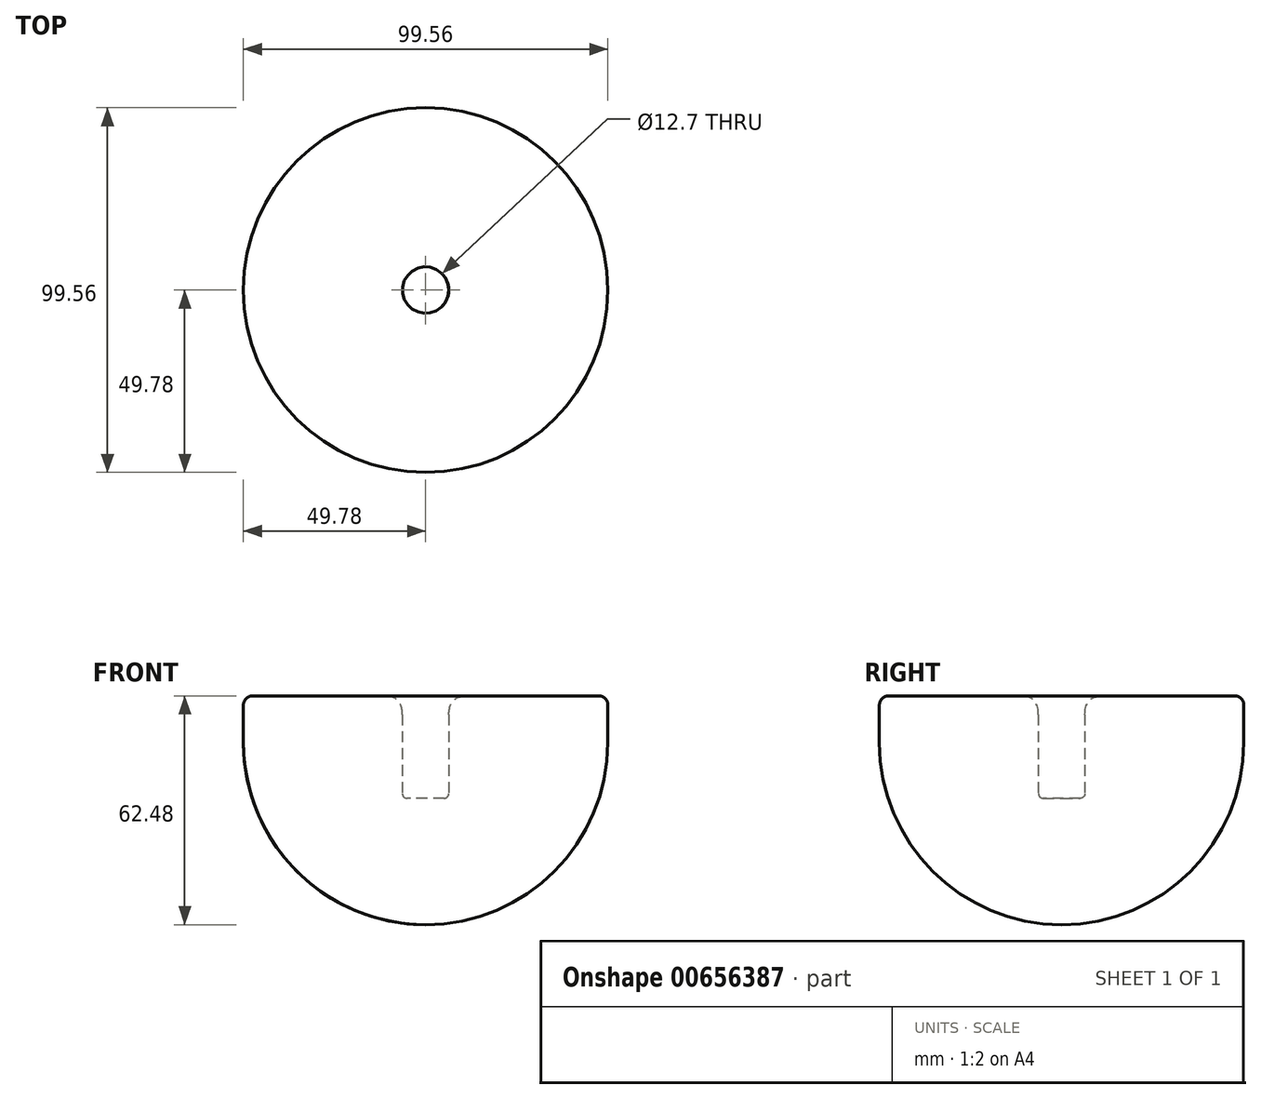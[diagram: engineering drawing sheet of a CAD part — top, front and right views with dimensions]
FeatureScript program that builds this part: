
annotation { "Feature Type Name" : "Feature", "Feature Type Description" : "" }
export const myFeature = defineFeature(function(context is Context, id is Id, definition is map)
    precondition{}
    {
        {
            var Q0;
            Q0=qCreatedBy(makeId("Front.planeOp"),FACE);
            var sketch = newSketch(context, id + "F0", { "sketchPlane" : qUnion([Q0])});
            skLineSegment(sketch, "E0", {"start": v(-49.78, 0) * mm, "end": v(0, 0) * mm});
            skArc(sketch, "E1", {"start": v(-49.78, 0) * mm, "mid": v(-35.2, -35.2) * mm, "end": v(0, -49.78) * mm});
            skLineSegment(sketch, "E2", {"start": v(0, 0) * mm, "end": v(0, -49.78) * mm});
            skSolve(sketch);
        }
        {
            var Q0;
            Q0=makeQuery(id+"F0.imprint","IMPRINT",FACE,{"disambiguationData":[TD([[makeQuery(id+"F0.imprint","IMPRINT",EDGE,{"derivedFrom":sQuery(id+"F0.wireOp",EDGE,"E0")}),-1.0]])]});
            var Q1;
            Q1=sQuery(id+"F0.wireOp",EDGE,"dce160f8-1f8b-4b9b-917d-d6703b323981");
            var Q2;
            Q2=sQuery(id+"F0.wireOp",EDGE,"E2");
            revolve(context, id + "F1", {"entities" : qUnion([Q0]), "surfaceEntities" : qUnion([Q1]), "axis" : qUnion([Q2]), "revolveType" : RevolveType.FULL, "oppositeDirection" : true});
        }
        {
            var Q0;
            Q0=makeQuery(id+"F1.opRevolve","SWEPT_FACE",FACE,{"disambiguationData":[OSD([sQuery(id+"F0.wireOp",EDGE,"E0")])]});
            var sketch = newSketch(context, id + "F2", { "sketchPlane" : qUnion([Q0])});
            skCircle(sketch, "E3", {"center": v(0, 0) * mm, "radius": 6.35 * mm});
            skSolve(sketch);
        }
        {
            var Q0;
            Q0=makeQuery(id+"F2.imprint","IMPRINT",FACE,{"disambiguationData":[TD([[makeQuery(id+"F2.imprint","IMPRINT",EDGE,{"derivedFrom":sQuery(id+"F2.wireOp",EDGE,"E3")}),-1.0]])]});
            var Q1;
            Q1=sQuery(id+"F2.wireOp",EDGE,"E3");
            extrude(context, id + "F3", {"entities" : qUnion([Q0]), "operationType" : NewBodyOperationType.ADD, "surfaceEntities" : qUnion([Q1]), "depth" : 12.7 * mm, "offsetDistance" : 25.4 * mm});
        }
        {
            var Q0;
            Q0=makeQuery(id+"F3.opExtrude","CAP_EDGE",EDGE,{"disambiguationData":[OSD([sQuery(id+"F0.wireOp",EDGE,"E0"),sQuery(id+"F0.wireOp",EDGE,"E1")])],"isStart":false});
            fillet(context, id + "F4", {"entities" : qUnion([Q0]), "radius" : 2.54 * mm, "allowEdgeOverflow" : false});
        }
        {
            var Q0;
            Q0=makeQuery(id+"F3.opExtrude","CAP_EDGE",EDGE,{"disambiguationData":[OSD([sQuery(id+"F2.wireOp",EDGE,"E3")])],"isStart":false});
            fillet(context, id + "F5", {"entities" : qUnion([Q0]), "radius" : 5.08 * mm, "tangentPropagation" : true, "rho" : 0.5, "crossSection" : FilletCrossSection.CONIC, "allowEdgeOverflow" : false});
        }
        {
            var Q0;
            Q0=makeQuery(id+"F1.opRevolve","SWEPT_FACE",FACE,{"disambiguationData":[OSD([sQuery(id+"F0.wireOp",EDGE,"E0")])]});
            extrude(context, id + "F6", {"entities" : qUnion([Q0]), "operationType" : NewBodyOperationType.REMOVE, "oppositeDirection" : true, "depth" : 15.24 * mm, "offsetDistance" : 25.4 * mm});
        }
        {
            var Q0;
            Q0=makeQuery(id+"F6.boolean.opBoolean","COPY",EDGE,{"derivedFrom":makeQuery(id+"F6.opExtrude","CAP_EDGE",EDGE,{"disambiguationData":[OSD([sQuery(id+"F2.wireOp",EDGE,"E3")])],"isStart":false})});
            fillet(context, id + "F7", {"entities" : qUnion([Q0]), "radius" : 1.27 * mm, "tangentPropagation" : true, "allowEdgeOverflow" : false});
        }
    });
